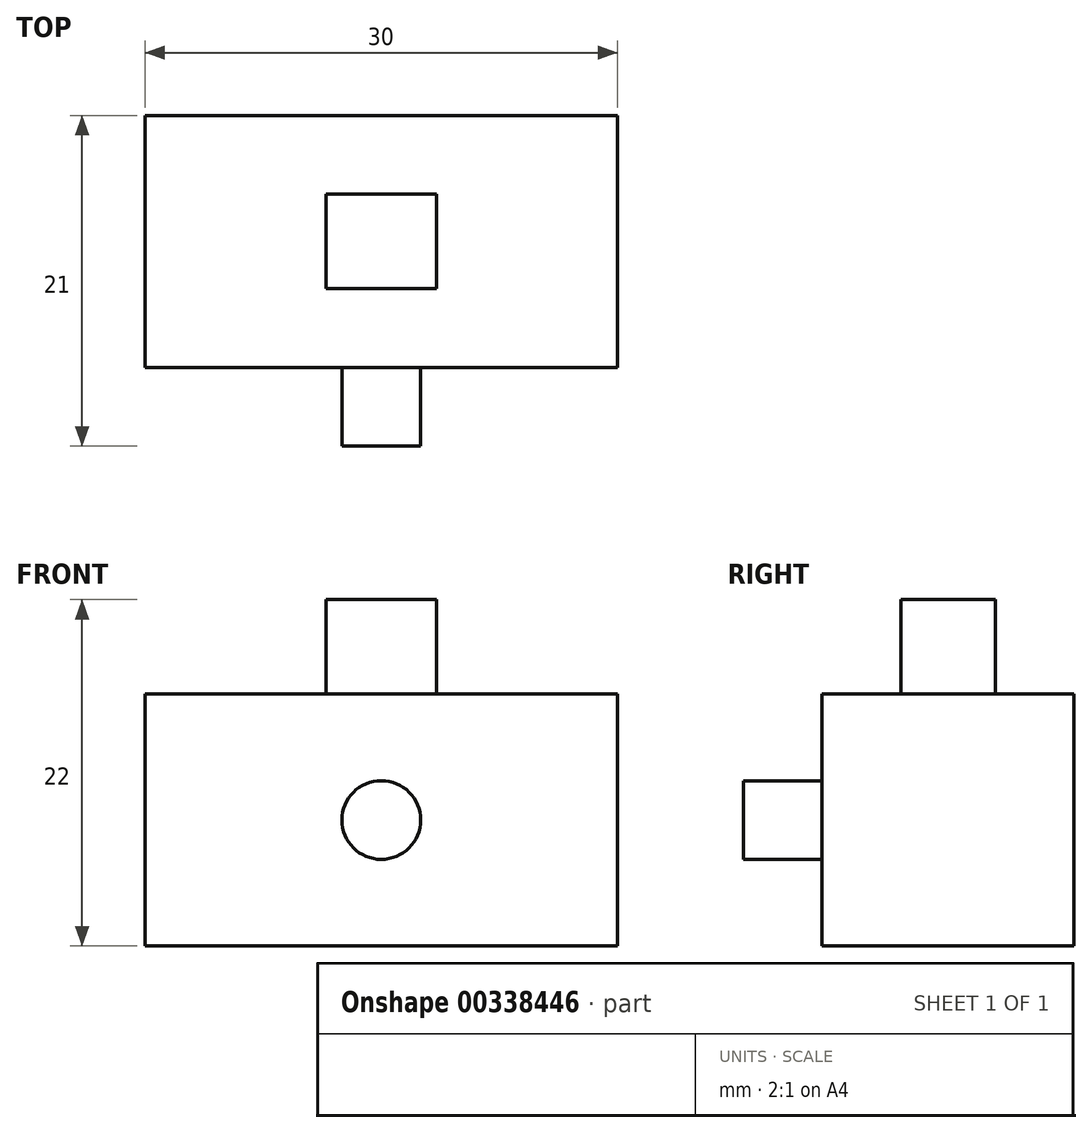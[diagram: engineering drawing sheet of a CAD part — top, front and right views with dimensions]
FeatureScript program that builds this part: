
annotation { "Feature Type Name" : "Feature", "Feature Type Description" : "" }
export const myFeature = defineFeature(function(context is Context, id is Id, definition is map)
    precondition{}
    {
        {
            var Q0;
            Q0=qCreatedBy(makeId("Top.planeOp"),FACE);
            var sketch = newSketch(context, id + "F0", { "sketchPlane" : qUnion([Q0])});
            skLineSegment(sketch, "E0.bottom", {"start": v(0, 0) * mm, "end": v(30, 0) * mm});
            skLineSegment(sketch, "E0.top", {"start": v(0, -16) * mm, "end": v(30, -16) * mm});
            skLineSegment(sketch, "E0.left", {"start": v(0, 0) * mm, "end": v(0, -16) * mm});
            skLineSegment(sketch, "E0.right", {"start": v(30, 0) * mm, "end": v(30, -16) * mm});
            skSolve(sketch);
        }
        {
            var Q0;
            Q0 = qSketchRegion(id + "F0", true);
            extrude(context, id + "F1", {"entities" : qUnion([Q0]), "depth" : 16 * mm});
        }
        {
            var Q0;
            Q0=makeQuery(id+"F1.opExtrude","CAP_FACE",FACE,{"disambiguationData":[OSD([sQuery(id+"F0.wireOp",EDGE,"E0.bottom"),sQuery(id+"F0.wireOp",EDGE,"E0.top"),sQuery(id+"F0.wireOp",EDGE,"E0.left"),sQuery(id+"F0.wireOp",EDGE,"E0.right")])],"isStart":false});
            var sketch = newSketch(context, id + "F2", { "sketchPlane" : qUnion([Q0])});
            skLineSegment(sketch, "E1.bottom", {"start": v(11.5, -5) * mm, "end": v(18.5, -5) * mm});
            skLineSegment(sketch, "E1.top", {"start": v(11.5, -11) * mm, "end": v(18.5, -11) * mm});
            skLineSegment(sketch, "E1.left", {"start": v(11.5, -5) * mm, "end": v(11.5, -11) * mm});
            skLineSegment(sketch, "E1.right", {"start": v(18.5, -5) * mm, "end": v(18.5, -11) * mm});
            skPoint(sketch, "E1.middle", {"position": v(15, -8) * mm});
            skPoint(sketch, "E1.middle.positionSnap0", {"position": v(30, -8) * mm});
            skPoint(sketch, "E1.middle.positionSnap1", {"position": v(15, 0) * mm});
            skPoint(sketch, "E1.centerSnap0", {"position": v(30, -8) * mm});
            skPoint(sketch, "E1.centerSnap1", {"position": v(15, 0) * mm});
            skSolve(sketch);
        }
        {
            var Q0;
            Q0 = qSketchRegion(id + "F2", true);
            extrude(context, id + "F3", {"entities" : qUnion([Q0]), "operationType" : NewBodyOperationType.ADD, "depth" : 6 * mm});
        }
        {
            var Q0;
            Q0=makeQuery(id+"F1.opExtrude","SWEPT_FACE",FACE,{"disambiguationData":[OSD([sQuery(id+"F0.wireOp",EDGE,"E0.top")])]});
            var sketch = newSketch(context, id + "F4", { "sketchPlane" : qUnion([Q0])});
            skCircle(sketch, "E2", {"center": v(15, 8) * mm, "radius": 2.5 * mm});
            skPoint(sketch, "E2.centerSnap0", {"position": v(30, 8) * mm});
            skPoint(sketch, "E2.centerSnap1", {"position": v(15, 16) * mm});
            skSolve(sketch);
        }
        {
            var Q0;
            Q0 = qSketchRegion(id + "F4", true);
            extrude(context, id + "F5", {"entities" : qUnion([Q0]), "operationType" : NewBodyOperationType.ADD, "depth" : 5 * mm});
        }
    });
